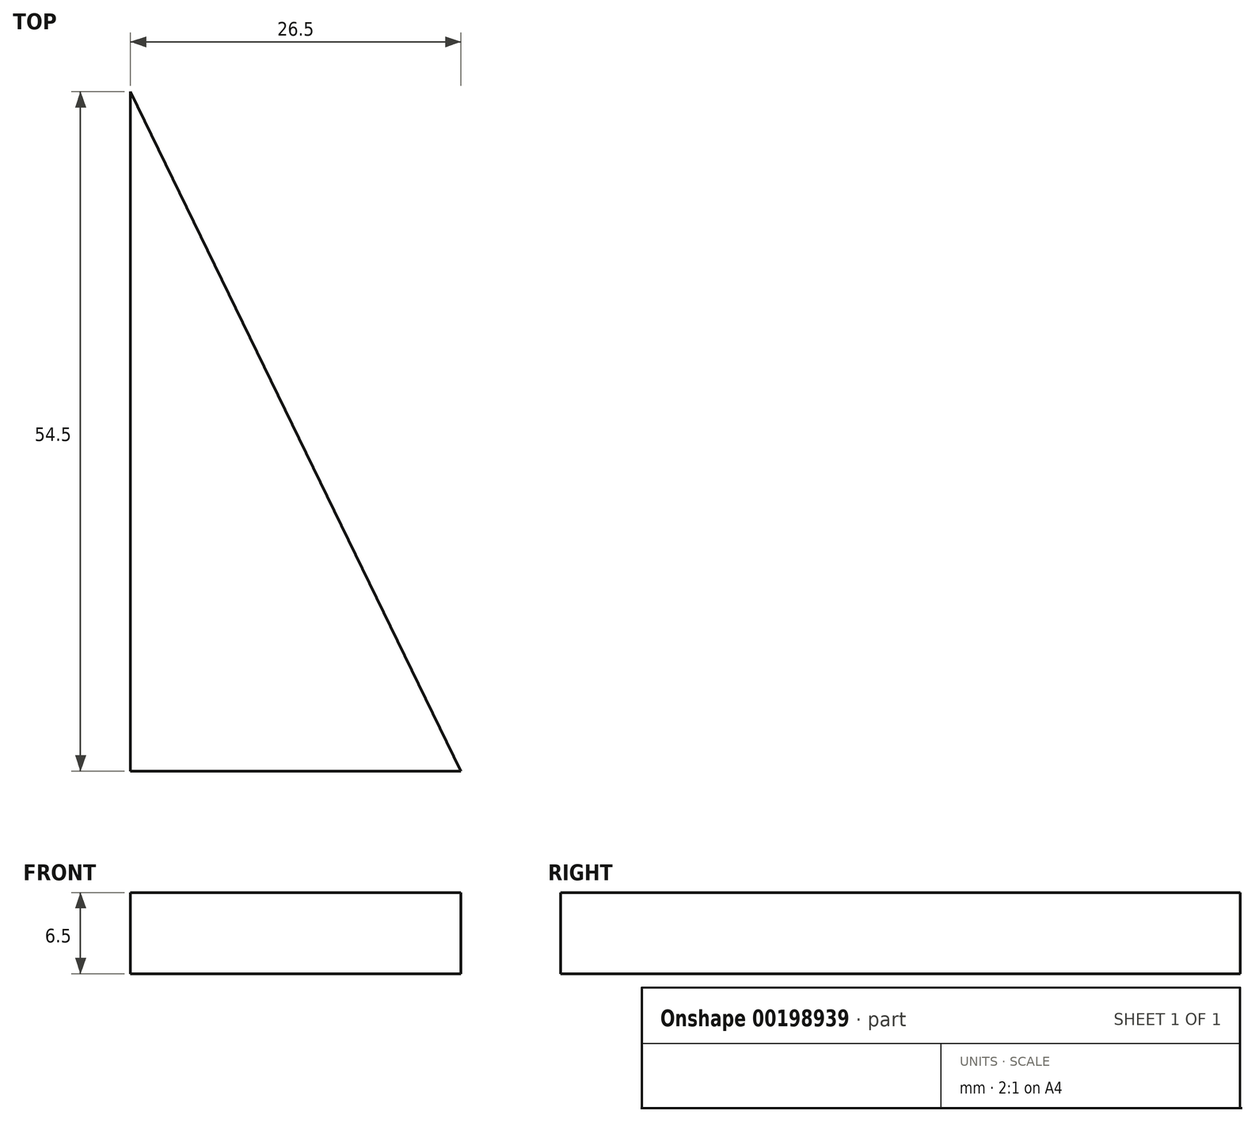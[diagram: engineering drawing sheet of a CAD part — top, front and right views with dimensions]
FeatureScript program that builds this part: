
annotation { "Feature Type Name" : "Feature", "Feature Type Description" : "" }
export const myFeature = defineFeature(function(context is Context, id is Id, definition is map)
    precondition{}
    {
        {
            var Q0;
            Q0=qCreatedBy(makeId("Top.planeOp"),FACE);
            var sketch = newSketch(context, id + "F0", { "sketchPlane" : qUnion([Q0])});
            skLineSegment(sketch, "E0", {"start": v(0, 54.5) * mm, "end": v(0, 0) * mm});
            skLineSegment(sketch, "E1", {"start": v(0, 0) * mm, "end": v(26.5, 0) * mm});
            skLineSegment(sketch, "E2", {"start": v(26.5, 0) * mm, "end": v(0, 54.5) * mm});
            skSolve(sketch);
        }
        {
            var Q0;
            Q0=makeQuery(id+"F0.imprint","IMPRINT",FACE,{"disambiguationData":[TD([[makeQuery(id+"F0.imprint","IMPRINT",EDGE,{"derivedFrom":sQuery(id+"F0.wireOp",EDGE,"E0")}),1.0]])]});
            extrude(context, id + "F1", {"entities" : qUnion([Q0]), "depth" : 6.5 * mm});
        }
    });
